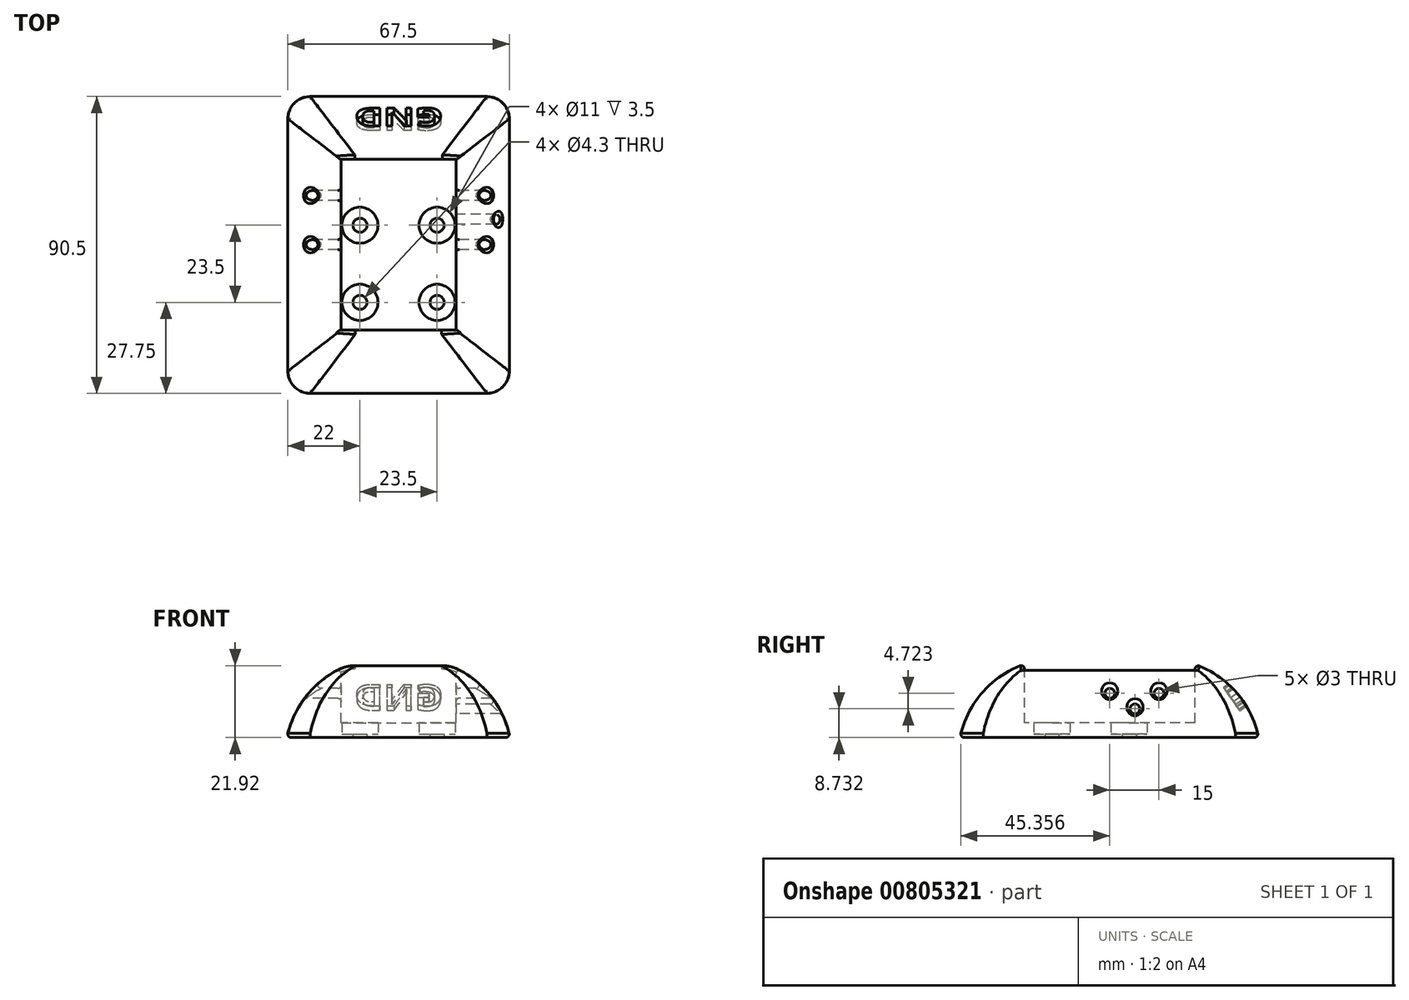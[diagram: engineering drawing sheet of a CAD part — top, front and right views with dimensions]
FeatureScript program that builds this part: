
annotation { "Feature Type Name" : "Feature", "Feature Type Description" : "" }
export const myFeature = defineFeature(function(context is Context, id is Id, definition is map)
    precondition{}
    {
        {
            var Q0;
            Q0=qCreatedBy(makeId("Top.planeOp"),FACE);
            var sketch = newSketch(context, id + "F0", { "sketchPlane" : qUnion([Q0])});
            skLineSegment(sketch, "E0.bottom", {"start": v(-34, 44) * mm, "end": v(34, 44) * mm});
            skLineSegment(sketch, "E0.top", {"start": v(-34, -47) * mm, "end": v(34, -47) * mm});
            skLineSegment(sketch, "E0.left", {"start": v(-34, 44) * mm, "end": v(-34, -47) * mm});
            skLineSegment(sketch, "E0.right", {"start": v(34, 44) * mm, "end": v(34, -47) * mm});
            skSolve(sketch);
        }
        {
            var Q0;
            Q0=makeQuery(id+"F0.imprint","IMPRINT",FACE,{"disambiguationData":[TD([[makeQuery(id+"F0.imprint","IMPRINT",EDGE,{"derivedFrom":sQuery(id+"F0.wireOp",EDGE,"E0.bottom")}),-1.0]])]});
            extrude(context, id + "F1", {"entities" : qUnion([Q0]), "depth" : 24 * mm, "offsetDistance" : 25 * mm});
        }
        {
            var Q0;
            Q0=makeQuery(id+"F1.opExtrude","CAP_EDGE",EDGE,{"disambiguationData":[OSD([sQuery(id+"F0.wireOp",EDGE,"E0.left")])],"isStart":false});
            var Q1;
            Q1=makeQuery(id+"F1.opExtrude","CAP_EDGE",EDGE,{"disambiguationData":[OSD([sQuery(id+"F0.wireOp",EDGE,"E0.top")])],"isStart":false});
            var Q2;
            Q2=makeQuery(id+"F1.opExtrude","CAP_EDGE",EDGE,{"disambiguationData":[OSD([sQuery(id+"F0.wireOp",EDGE,"E0.right")])],"isStart":false});
            var Q3;
            Q3=makeQuery(id+"F1.opExtrude","CAP_EDGE",EDGE,{"disambiguationData":[OSD([sQuery(id+"F0.wireOp",EDGE,"E0.bottom")])],"isStart":false});
            fillet(context, id + "F2", {"entities" : qUnion([Q0, Q1, Q2, Q3]), "radius" : 30 * mm, "tangentPropagation" : true, "allowEdgeOverflow" : false});
        }
        {
            var Q0;
            Q0=makeQuery(id+"F2.opFillet","BLEND_EDGE",EDGE,{"blendedFrom":[makeQuery(id+"F1.opExtrude","CAP_EDGE",EDGE,{"disambiguationData":[OSD([sQuery(id+"F0.wireOp",EDGE,"E0.bottom")])],"isStart":false}),makeQuery(id+"F1.opExtrude","CAP_EDGE",EDGE,{"disambiguationData":[OSD([sQuery(id+"F0.wireOp",EDGE,"E0.left")])],"isStart":false})],"blendedInto":[]});
            var Q1;
            Q1=makeQuery(id+"F2.opFillet","BLEND_EDGE",EDGE,{"blendedFrom":[makeQuery(id+"F1.opExtrude","CAP_EDGE",EDGE,{"disambiguationData":[OSD([sQuery(id+"F0.wireOp",EDGE,"E0.top")])],"isStart":false}),makeQuery(id+"F1.opExtrude","CAP_EDGE",EDGE,{"disambiguationData":[OSD([sQuery(id+"F0.wireOp",EDGE,"E0.left")])],"isStart":false})],"blendedInto":[]});
            var Q2;
            Q2=makeQuery(id+"F2.opFillet","BLEND_EDGE",EDGE,{"blendedFrom":[makeQuery(id+"F1.opExtrude","CAP_EDGE",EDGE,{"disambiguationData":[OSD([sQuery(id+"F0.wireOp",EDGE,"E0.top")])],"isStart":false}),makeQuery(id+"F1.opExtrude","CAP_EDGE",EDGE,{"disambiguationData":[OSD([sQuery(id+"F0.wireOp",EDGE,"E0.right")])],"isStart":false})],"blendedInto":[]});
            var Q3;
            Q3=makeQuery(id+"F2.opFillet","BLEND_EDGE",EDGE,{"blendedFrom":[makeQuery(id+"F1.opExtrude","CAP_EDGE",EDGE,{"disambiguationData":[OSD([sQuery(id+"F0.wireOp",EDGE,"E0.bottom")])],"isStart":false}),makeQuery(id+"F1.opExtrude","CAP_EDGE",EDGE,{"disambiguationData":[OSD([sQuery(id+"F0.wireOp",EDGE,"E0.right")])],"isStart":false})],"blendedInto":[]});
            fillet(context, id + "F3", {"entities" : qUnion([Q0, Q1, Q2, Q3]), "radius" : 7 * mm, "tangentPropagation" : true, "allowEdgeOverflow" : false});
        }
        {
            var Q0;
            Q0=makeQuery(id+"F1.opExtrude","CAP_FACE",FACE,{"disambiguationData":[OSD([sQuery(id+"F0.wireOp",EDGE,"E0.bottom"),sQuery(id+"F0.wireOp",EDGE,"E0.top"),sQuery(id+"F0.wireOp",EDGE,"E0.left"),sQuery(id+"F0.wireOp",EDGE,"E0.right")])],"isStart":true});
            var sketch = newSketch(context, id + "F4", { "sketchPlane" : qUnion([Q0])});
            skCircle(sketch, "E1", {"center": v(-11.75, 19) * mm, "radius": 2.15 * mm});
            skCircle(sketch, "E2", {"center": v(-11.75, -4.5) * mm, "radius": 2.15 * mm});
            skCircle(sketch, "E3", {"center": v(11.75, 19) * mm, "radius": 2.15 * mm});
            skCircle(sketch, "E4", {"center": v(11.75, -4.5) * mm, "radius": 2.15 * mm});
            skCircle(sketch, "E5", {"center": v(-11.75, 19) * mm, "radius": 5.5 * mm});
            skCircle(sketch, "E6", {"center": v(11.75, 19) * mm, "radius": 5.5 * mm});
            skCircle(sketch, "E7", {"center": v(11.75, -4.5) * mm, "radius": 5.5 * mm});
            skCircle(sketch, "E8", {"center": v(-11.75, -4.5) * mm, "radius": 5.5 * mm});
            skSolve(sketch);
        }
        {
            var Q0;
            Q0=makeQuery(id+"F4.imprint","IMPRINT",FACE,{"disambiguationData":[TD([[makeQuery(id+"F4.imprint","IMPRINT",EDGE,{"derivedFrom":sQuery(id+"F4.wireOp",EDGE,"E1")}),1.0]])]});
            var Q1;
            Q1=makeQuery(id+"F4.imprint","IMPRINT",FACE,{"disambiguationData":[TD([[makeQuery(id+"F4.imprint","IMPRINT",EDGE,{"derivedFrom":sQuery(id+"F4.wireOp",EDGE,"E3")}),1.0]])]});
            var Q2;
            Q2=makeQuery(id+"F4.imprint","IMPRINT",FACE,{"disambiguationData":[TD([[makeQuery(id+"F4.imprint","IMPRINT",EDGE,{"derivedFrom":sQuery(id+"F4.wireOp",EDGE,"E4")}),1.0]])]});
            var Q3;
            Q3=makeQuery(id+"F4.imprint","IMPRINT",FACE,{"disambiguationData":[TD([[makeQuery(id+"F4.imprint","IMPRINT",EDGE,{"derivedFrom":sQuery(id+"F4.wireOp",EDGE,"E2")}),1.0]])]});
            var Q4;
            Q4=makeQuery(id+"F4.imprint","IMPRINT",FACE,{"disambiguationData":[TD([[makeQuery(id+"F4.imprint","IMPRINT",EDGE,{"derivedFrom":sQuery(id+"F4.wireOp",EDGE,"E1")}),-1.0]])]});
            var Q5;
            Q5=makeQuery(id+"F4.imprint","IMPRINT",FACE,{"disambiguationData":[TD([[makeQuery(id+"F4.imprint","IMPRINT",EDGE,{"derivedFrom":sQuery(id+"F4.wireOp",EDGE,"E3")}),-1.0]])]});
            var Q6;
            Q6=makeQuery(id+"F4.imprint","IMPRINT",FACE,{"disambiguationData":[TD([[makeQuery(id+"F4.imprint","IMPRINT",EDGE,{"derivedFrom":sQuery(id+"F4.wireOp",EDGE,"E4")}),-1.0]])]});
            var Q7;
            Q7=makeQuery(id+"F4.imprint","IMPRINT",FACE,{"disambiguationData":[TD([[makeQuery(id+"F4.imprint","IMPRINT",EDGE,{"derivedFrom":sQuery(id+"F4.wireOp",EDGE,"E2")}),-1.0]])]});
            extrude(context, id + "F5", {"entities" : qUnion([Q0, Q1, Q2, Q3, Q4, Q5, Q6, Q7]), "operationType" : NewBodyOperationType.REMOVE, "oppositeDirection" : true, "depth" : 25 * mm, "offsetDistance" : 25 * mm, "hasSecondDirection" : true, "secondDirectionOppositeDirection" : true, "secondDirectionDepth" : 1 * mm});
        }
        {
            var Q0;
            Q0=makeQuery(id+"F4.imprint","IMPRINT",FACE,{"disambiguationData":[TD([[makeQuery(id+"F4.imprint","IMPRINT",EDGE,{"derivedFrom":sQuery(id+"F4.wireOp",EDGE,"E1")}),1.0]])]});
            var Q1;
            Q1=makeQuery(id+"F4.imprint","IMPRINT",FACE,{"disambiguationData":[TD([[makeQuery(id+"F4.imprint","IMPRINT",EDGE,{"derivedFrom":sQuery(id+"F4.wireOp",EDGE,"E3")}),1.0]])]});
            var Q2;
            Q2=makeQuery(id+"F4.imprint","IMPRINT",FACE,{"disambiguationData":[TD([[makeQuery(id+"F4.imprint","IMPRINT",EDGE,{"derivedFrom":sQuery(id+"F4.wireOp",EDGE,"E2")}),1.0]])]});
            var Q3;
            Q3=makeQuery(id+"F4.imprint","IMPRINT",FACE,{"disambiguationData":[TD([[makeQuery(id+"F4.imprint","IMPRINT",EDGE,{"derivedFrom":sQuery(id+"F4.wireOp",EDGE,"E4")}),1.0]])]});
            extrude(context, id + "F6", {"entities" : qUnion([Q0, Q1, Q2, Q3]), "operationType" : NewBodyOperationType.REMOVE, "oppositeDirection" : true, "depth" : 25 * mm, "offsetDistance" : 25 * mm});
        }
        {
            var Q0;
            {var subQ0=sQuery(id+"F0.wireOp",EDGE,"E0.bottom");Q0=makeQuery(id+"FgaABafQtbcfGWg_1.opChamfer","BLEND_EDGE",EDGE,{"blendedFrom":[makeQuery(id+"F2.opFillet","BLEND_EDGE",EDGE,{"blendedFrom":[makeQuery(id+"F1.opExtrude","CAP_EDGE",EDGE,{"disambiguationData":[OSD([subQ0])],"isStart":false}),makeQuery(id+"F1.opExtrude","CAP_FACE",FACE,{"disambiguationData":[OSD([subQ0,sQuery(id+"F0.wireOp",EDGE,"E0.top"),sQuery(id+"F0.wireOp",EDGE,"E0.left"),sQuery(id+"F0.wireOp",EDGE,"E0.right")])],"isStart":true})],"blendedInto":[makeQuery(id+"F1.opExtrude","CAP_FACE",FACE,{"disambiguationData":[OSD([subQ0,sQuery(id+"F0.wireOp",EDGE,"E0.top"),sQuery(id+"F0.wireOp",EDGE,"E0.left"),sQuery(id+"F0.wireOp",EDGE,"E0.right")])],"isStart":true})]}),makeQuery(id+"F2.opFillet","BLEND_FACE",FACE,{"disambiguationData":[OSD([subQ0])]})],"blendedInto":[makeQuery(id+"F2.opFillet","BLEND_FACE",FACE,{"disambiguationData":[OSD([subQ0])]})]});}
            var Q1;
            {var subQ0=sQuery(id+"F0.wireOp",EDGE,"E0.bottom");Q1=makeQuery(id+"F2.opFillet","BLEND_EDGE",EDGE,{"blendedFrom":[makeQuery(id+"F1.opExtrude","CAP_EDGE",EDGE,{"disambiguationData":[OSD([subQ0])],"isStart":false}),makeQuery(id+"F1.opExtrude","CAP_FACE",FACE,{"disambiguationData":[OSD([subQ0,sQuery(id+"F0.wireOp",EDGE,"E0.top"),sQuery(id+"F0.wireOp",EDGE,"E0.left"),sQuery(id+"F0.wireOp",EDGE,"E0.right")])],"isStart":true})],"blendedInto":[makeQuery(id+"F1.opExtrude","CAP_FACE",FACE,{"disambiguationData":[OSD([subQ0,sQuery(id+"F0.wireOp",EDGE,"E0.top"),sQuery(id+"F0.wireOp",EDGE,"E0.left"),sQuery(id+"F0.wireOp",EDGE,"E0.right")])],"isStart":true})]});}
            cPlane(context, id + "F7", {"entities" : qUnion([Q0, Q1]), "cplaneType" : CPlaneType.LINE_ANGLE, "offset" : 25 * mm, "angle" : 35 * degree, "width" : 150 * mm, "height" : 150 * mm});
        }
        {
            var Q0;
            Q0=qCreatedBy(id+"F7.planeOp",FACE);
            var sketch = newSketch(context, id + "F8", { "sketchPlane" : qUnion([Q0])});
            skText(sketch, "E9", { "text": "GND", "fontName": "OpenSans-Bold.ttf"});
            const initialGuessF8  = {"E9": [-0.0135, -0.01516, 1, 0, 0.00851]};
            skSetInitialGuess(sketch, initialGuessF8);
            skSolve(sketch);
        }
        {
            var Q0;
            Q0 = qSketchRegion(id + "F8", true);
            extrude(context, id + "F9", {"entities" : qUnion([Q0]), "operationType" : NewBodyOperationType.REMOVE, "depth" : 25 * mm, "offsetDistance" : 25 * mm});
        }
        {
            var Q0;
            Q0=makeQuery(id+"F1.opExtrude","CAP_FACE",FACE,{"disambiguationData":[OSD([sQuery(id+"F0.wireOp",EDGE,"E0.bottom"),sQuery(id+"F0.wireOp",EDGE,"E0.top"),sQuery(id+"F0.wireOp",EDGE,"E0.left"),sQuery(id+"F0.wireOp",EDGE,"E0.right")])],"isStart":false});
            var sketch = newSketch(context, id + "F10", { "sketchPlane" : qUnion([Q0])});
            skLineSegment(sketch, "E10.bottom", {"start": v(-17.5, 24.6) * mm, "end": v(17.5, 24.6) * mm});
            skLineSegment(sketch, "E10.top", {"start": v(-17.5, -27.4) * mm, "end": v(17.5, -27.4) * mm});
            skLineSegment(sketch, "E10.left", {"start": v(-17.5, 24.6) * mm, "end": v(-17.5, -27.4) * mm});
            skLineSegment(sketch, "E10.right", {"start": v(17.5, 24.6) * mm, "end": v(17.5, -27.4) * mm});
            skSolve(sketch);
        }
        {
            var Q0;
            Q0=makeQuery(id+"F10.imprint","IMPRINT",FACE,{"disambiguationData":[TD([[makeQuery(id+"F10.imprint","IMPRINT",EDGE,{"derivedFrom":sQuery(id+"F10.wireOp",EDGE,"E10.bottom")}),-1.0]])]});
            var Q1;
            {var subQ0=sQuery(id+"F0.wireOp",EDGE,"E0.right");var subQ1=sQuery(id+"F0.wireOp",EDGE,"E0.left");var subQ2=sQuery(id+"F0.wireOp",EDGE,"E0.top");var subQ3=sQuery(id+"F0.wireOp",EDGE,"E0.bottom");var subQ4=makeQuery(id+"F1.opExtrude","CAP_FACE",FACE,{"disambiguationData":[OSD([subQ3,subQ2,subQ1,subQ0])],"isStart":false});Q1=makeQuery(id+"F10.imprint","IMPRINT",FACE,{"disambiguationData":[TD([[makeQuery(id+"F10.imprint","IMPRINT",EDGE,{"derivedFrom":makeQuery(id+"F2.opFillet","BLEND_EDGE",EDGE,{"blendedFrom":[makeQuery(id+"F1.opExtrude","CAP_EDGE",EDGE,{"disambiguationData":[OSD([subQ3])],"isStart":false}),subQ4],"blendedInto":[subQ4]})}),1.0]])]});}
            extrude(context, id + "F11", {"entities" : qUnion([Q0, Q1]), "operationType" : NewBodyOperationType.REMOVE, "oppositeDirection" : true, "depth" : 19.5 * mm, "offsetDistance" : 25 * mm});
        }
        {
            var Q0;
            Q0=makeQuery(id+"F11.boolean.opBoolean","COPY",FACE,{"derivedFrom":makeQuery(id+"F11.opExtrude","SWEPT_FACE",FACE,{"disambiguationData":[OSD([sQuery(id+"F10.wireOp",EDGE,"E10.right")])]})});
            var sketch = newSketch(context, id + "F12", { "sketchPlane" : qUnion([Q0])});
            skCircle(sketch, "E11", {"center": v(1.4, 13.46) * mm, "radius": 1.5 * mm});
            skCircle(sketch, "E12", {"center": v(-13.6, 13.46) * mm, "radius": 1.5 * mm});
            skCircle(sketch, "E13", {"center": v(-6.3, 8.73) * mm, "radius": 1.5 * mm});
            skSolve(sketch);
        }
        {
            var Q0;
            Q0=makeQuery(id+"F12.imprint","IMPRINT",FACE,{"disambiguationData":[TD([[makeQuery(id+"F12.imprint","IMPRINT",EDGE,{"derivedFrom":sQuery(id+"F12.wireOp",EDGE,"E12")}),1.0]])]});
            var Q1;
            Q1=makeQuery(id+"F12.imprint","IMPRINT",FACE,{"disambiguationData":[TD([[makeQuery(id+"F12.imprint","IMPRINT",EDGE,{"derivedFrom":sQuery(id+"F12.wireOp",EDGE,"E11")}),1.0]])]});
            extrude(context, id + "F13", {"entities" : qUnion([Q0, Q1]), "operationType" : NewBodyOperationType.REMOVE, "endBound" : BoundingType.THROUGH_ALL, "oppositeDirection" : true, "depth" : 25 * mm, "offsetDistance" : 25 * mm, "hasSecondDirection" : true, "secondDirectionOppositeDirection" : false, "secondDirectionDepth" : 71.9 * mm});
        }
        {
            var Q0;
            Q0=makeQuery(id+"F12.imprint","IMPRINT",FACE,{"disambiguationData":[TD([[makeQuery(id+"F12.imprint","IMPRINT",EDGE,{"derivedFrom":sQuery(id+"F12.wireOp",EDGE,"E13")}),1.0]])]});
            extrude(context, id + "F14", {"entities" : qUnion([Q0]), "operationType" : NewBodyOperationType.REMOVE, "oppositeDirection" : true, "depth" : 25 * mm, "offsetDistance" : 25 * mm});
        }
        {
            var Q0;
            {var subQ1=sQuery(id+"F0.wireOp",EDGE,"E0.left");var subQ3=sQuery(id+"F0.wireOp",EDGE,"E0.bottom");Q0=makeQuery(id+"F11.boolean.opBoolean","INTERSECT",EDGE,{"derivedFrom":[makeQuery(id+"F9.boolean.opBoolean","SPLIT",FACE,{"disambiguationData":[TD([makeQuery(id+"F2.opFillet","BLEND_FACE",FACE,{"disambiguationData":[OSD([subQ1])]})])],"derivedFrom":makeQuery(id+"F2.opFillet","BLEND_FACE",FACE,{"disambiguationData":[OSD([subQ3])]})}),makeQuery(id+"F11.opExtrude","SWEPT_FACE",FACE,{"disambiguationData":[OSD([sQuery(id+"F10.wireOp",EDGE,"E10.bottom")])]})]});}
            var Q1;
            Q1=makeQuery(id+"F11.boolean.opBoolean","INTERSECT",EDGE,{"derivedFrom":[makeQuery(id+"F2.opFillet","BLEND_FACE",FACE,{"disambiguationData":[OSD([sQuery(id+"F0.wireOp",EDGE,"E0.left")])]}),makeQuery(id+"F11.opExtrude","SWEPT_FACE",FACE,{"disambiguationData":[OSD([sQuery(id+"F10.wireOp",EDGE,"E10.left")])]})]});
            var Q2;
            Q2=makeQuery(id+"F11.boolean.opBoolean","INTERSECT",EDGE,{"derivedFrom":[makeQuery(id+"F2.opFillet","BLEND_FACE",FACE,{"disambiguationData":[OSD([sQuery(id+"F0.wireOp",EDGE,"E0.right")])]}),makeQuery(id+"F11.opExtrude","SWEPT_FACE",FACE,{"disambiguationData":[OSD([sQuery(id+"F10.wireOp",EDGE,"E10.right")])]})]});
            var Q3;
            Q3=makeQuery(id+"F11.boolean.opBoolean","INTERSECT",EDGE,{"derivedFrom":[makeQuery(id+"F2.opFillet","BLEND_FACE",FACE,{"disambiguationData":[OSD([sQuery(id+"F0.wireOp",EDGE,"E0.top")])]}),makeQuery(id+"F11.opExtrude","SWEPT_FACE",FACE,{"disambiguationData":[OSD([sQuery(id+"F10.wireOp",EDGE,"E10.top")])]})]});
            fillet(context, id + "F15", {"entities" : qUnion([Q0, Q1, Q2, Q3]), "radius" : 1 * mm, "tangentPropagation" : true, "allowEdgeOverflow" : false});
        }
        {
            var Q0;
            Q0=makeQuery(id+"F13.boolean.opBoolean","INTERSECT",EDGE,{"derivedFrom":[makeQuery(id+"F11.boolean.opBoolean","COPY",FACE,{"derivedFrom":makeQuery(id+"F11.opExtrude","SWEPT_FACE",FACE,{"disambiguationData":[OSD([sQuery(id+"F10.wireOp",EDGE,"E10.left")])]})}),makeQuery(id+"F13.opExtrude","SWEPT_FACE",FACE,{"disambiguationData":[OSD([sQuery(id+"F12.wireOp",EDGE,"E11")])]})]});
            var Q1;
            Q1=makeQuery(id+"F13.boolean.opBoolean","INTERSECT",EDGE,{"derivedFrom":[makeQuery(id+"F11.boolean.opBoolean","COPY",FACE,{"derivedFrom":makeQuery(id+"F11.opExtrude","SWEPT_FACE",FACE,{"disambiguationData":[OSD([sQuery(id+"F10.wireOp",EDGE,"E10.left")])]})}),makeQuery(id+"F13.opExtrude","SWEPT_FACE",FACE,{"disambiguationData":[OSD([sQuery(id+"F12.wireOp",EDGE,"E12")])]})]});
            var Q2;
            Q2=makeQuery(id+"F13.boolean.opBoolean","INTERSECT",EDGE,{"derivedFrom":[makeQuery(id+"F2.opFillet","BLEND_FACE",FACE,{"disambiguationData":[OSD([sQuery(id+"F0.wireOp",EDGE,"E0.right")])]}),makeQuery(id+"F13.opExtrude","SWEPT_FACE",FACE,{"disambiguationData":[OSD([sQuery(id+"F12.wireOp",EDGE,"E12")])]})]});
            var Q3;
            Q3=makeQuery(id+"F13.boolean.opBoolean","INTERSECT",EDGE,{"derivedFrom":[makeQuery(id+"F2.opFillet","BLEND_FACE",FACE,{"disambiguationData":[OSD([sQuery(id+"F0.wireOp",EDGE,"E0.right")])]}),makeQuery(id+"F13.opExtrude","SWEPT_FACE",FACE,{"disambiguationData":[OSD([sQuery(id+"F12.wireOp",EDGE,"E11")])]})]});
            var Q4;
            Q4=makeQuery(id+"F13.boolean.opBoolean","INTERSECT",EDGE,{"derivedFrom":[makeQuery(id+"F11.boolean.opBoolean","COPY",FACE,{"derivedFrom":makeQuery(id+"F11.opExtrude","SWEPT_FACE",FACE,{"disambiguationData":[OSD([sQuery(id+"F10.wireOp",EDGE,"E10.right")])]})}),makeQuery(id+"F13.opExtrude","SWEPT_FACE",FACE,{"disambiguationData":[OSD([sQuery(id+"F12.wireOp",EDGE,"E11")])]})]});
            var Q5;
            Q5=makeQuery(id+"F13.boolean.opBoolean","INTERSECT",EDGE,{"derivedFrom":[makeQuery(id+"F11.boolean.opBoolean","COPY",FACE,{"derivedFrom":makeQuery(id+"F11.opExtrude","SWEPT_FACE",FACE,{"disambiguationData":[OSD([sQuery(id+"F10.wireOp",EDGE,"E10.right")])]})}),makeQuery(id+"F13.opExtrude","SWEPT_FACE",FACE,{"disambiguationData":[OSD([sQuery(id+"F12.wireOp",EDGE,"E12")])]})]});
            var Q6;
            Q6=makeQuery(id+"F13.boolean.opBoolean","INTERSECT",EDGE,{"derivedFrom":[makeQuery(id+"F2.opFillet","BLEND_FACE",FACE,{"disambiguationData":[OSD([sQuery(id+"F0.wireOp",EDGE,"E0.left")])]}),makeQuery(id+"F13.opExtrude","SWEPT_FACE",FACE,{"disambiguationData":[OSD([sQuery(id+"F12.wireOp",EDGE,"E12")])]})]});
            var Q7;
            Q7=makeQuery(id+"F2.opFillet","BLEND_FACE",FACE,{"disambiguationData":[OSD([sQuery(id+"F0.wireOp",EDGE,"E0.left")])]});
            var Q8;
            Q8=makeQuery(id+"F14.boolean.opBoolean","INTERSECT",EDGE,{"derivedFrom":[makeQuery(id+"F2.opFillet","BLEND_FACE",FACE,{"disambiguationData":[OSD([sQuery(id+"F0.wireOp",EDGE,"E0.right")])]}),makeQuery(id+"F14.opExtrude","SWEPT_FACE",FACE,{"disambiguationData":[OSD([sQuery(id+"F12.wireOp",EDGE,"E13")])]})]});
            var Q9;
            Q9=makeQuery(id+"F14.boolean.opBoolean","COPY",EDGE,{"derivedFrom":makeQuery(id+"F14.opExtrude","CAP_EDGE",EDGE,{"disambiguationData":[OSD([sQuery(id+"F12.wireOp",EDGE,"E13")])],"isStart":true})});
            fillet(context, id + "F16", {"entities" : qUnion([Q0, Q1, Q2, Q3, Q4, Q5, Q6, Q7, Q8, Q9]), "radius" : 1 * mm, "tangentPropagation" : true, "allowEdgeOverflow" : false});
        }
    });
